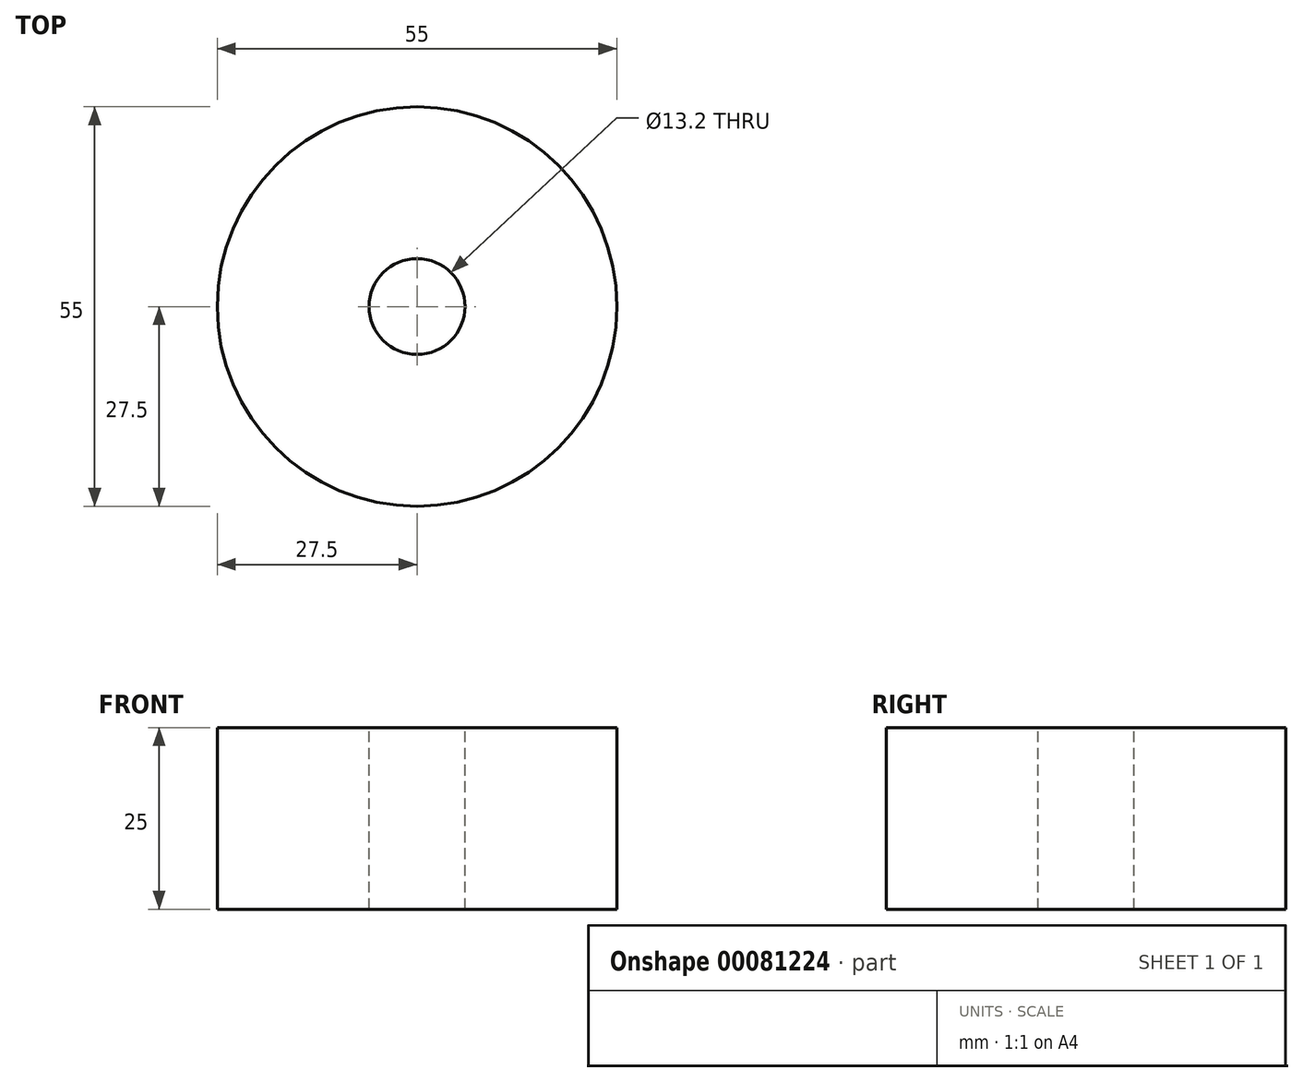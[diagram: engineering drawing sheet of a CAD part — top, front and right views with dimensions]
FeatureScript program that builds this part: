
annotation { "Feature Type Name" : "Feature", "Feature Type Description" : "" }
export const myFeature = defineFeature(function(context is Context, id is Id, definition is map)
    precondition{}
    {
        {
            var Q0;
            Q0=qCreatedBy(makeId("Top.planeOp"),FACE);
            var sketch = newSketch(context, id + "F0", { "sketchPlane" : qUnion([Q0])});
            skCircle(sketch, "E0", {"center": v(0, 0) * mm, "radius": 27.5 * mm});
            skSolve(sketch);
        }
        {
            var Q0;
            Q0=makeQuery(id+"F0.imprint","IMPRINT",FACE,{"disambiguationData":[TD([[makeQuery(id+"F0.imprint","IMPRINT",EDGE,{"derivedFrom":sQuery(id+"F0.wireOp",EDGE,"E0")}),1.0]])]});
            extrude(context, id + "F1", {"entities" : qUnion([Q0]), "depth" : 25 * mm});
        }
        {
            var Q0;
            Q0=sQuery(id+"F0.wireOp",VERTEX,"E0.center");
            var Q1;
            Q1=makeQuery(id+"F1.opExtrude","SWEPT_BODY",BODY,{"disambiguationData":[OSD([sQuery(id+"F0.wireOp",EDGE,"E0")])]});
            hole(context, id + "F2", {"style" : HoleStyle.SIMPLE, "endStyle" : HoleEndStyle.THROUGH, "oppositeDirection" : true, "standardTappedOrClearance" : lookupTablePath({ "standard" : "ISO", "fit" : "Normal", "size" : "M12", "type" : "Clearance" }), "standardBlindInLast" : lookupTablePath({ "fit" : "Standard", "standard" : "ISO", "size" : "M12", "type" : "Clearance" }), "holeDiameter" : 13.2 * mm, "locations" : qUnion([Q0]), "scope" : qUnion([Q1]), "isTappedThrough" : true, "startStyle" : HoleStartStyle.PART});
        }
    });
